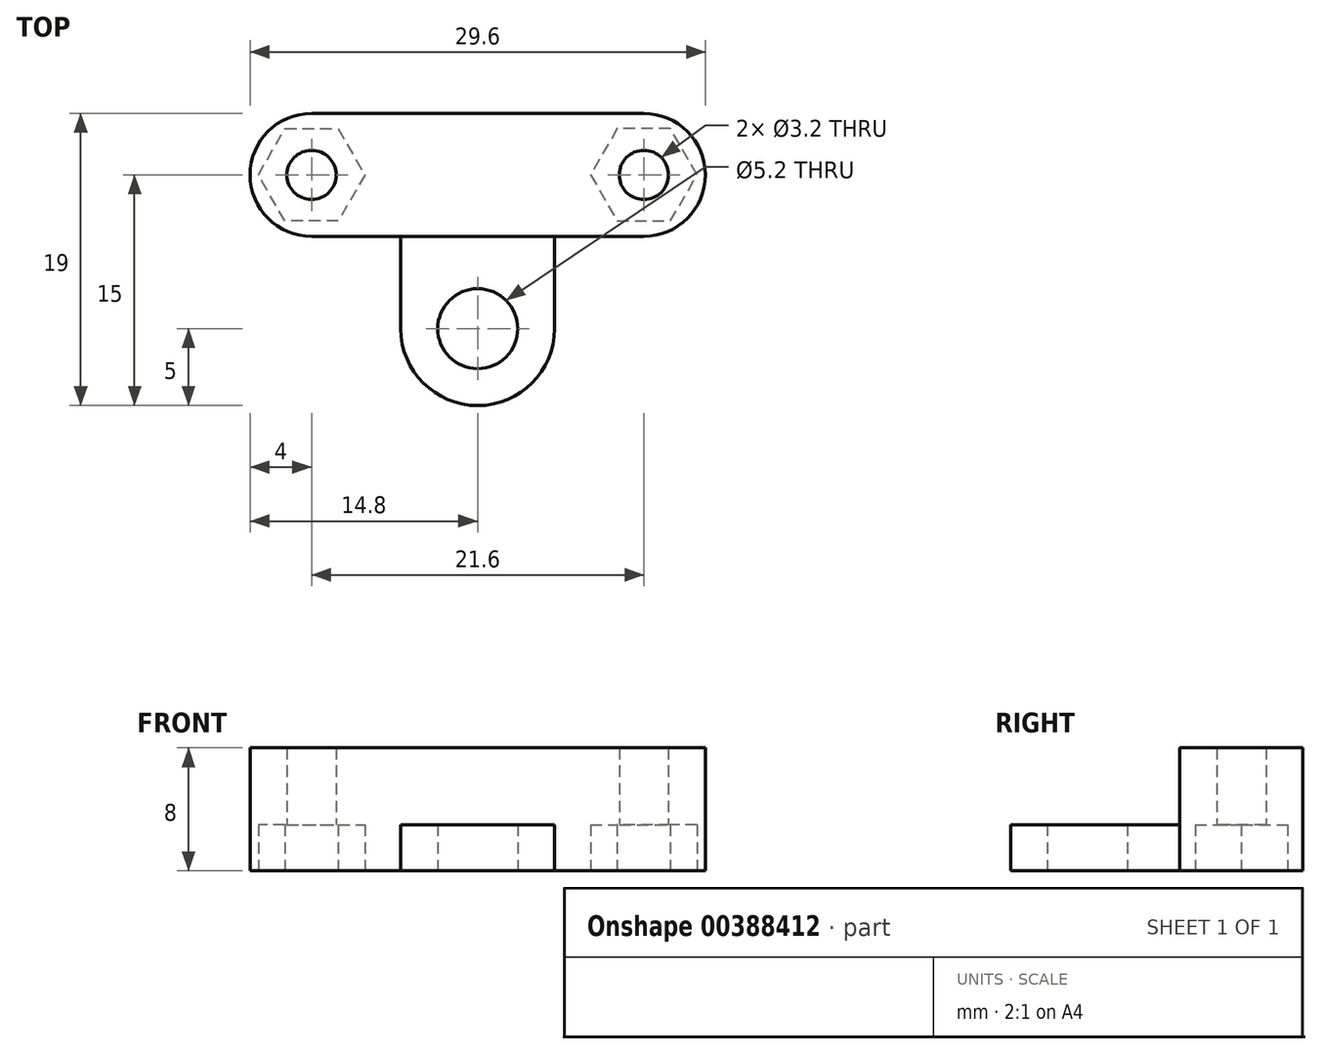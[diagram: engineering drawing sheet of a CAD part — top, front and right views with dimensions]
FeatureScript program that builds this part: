
annotation { "Feature Type Name" : "Feature", "Feature Type Description" : "" }
export const myFeature = defineFeature(function(context is Context, id is Id, definition is map)
    precondition{}
    {
        {
            var Q0;
            Q0=qCreatedBy(makeId("Top.planeOp"),FACE);
            var sketch = newSketch(context, id + "F0", { "sketchPlane" : qUnion([Q0])});
            skCircle(sketch, "E0", {"center": v(0, 0) * mm, "radius": 2.6 * mm});
            skArc(sketch, "E1", {"start": v(-5, 0) * mm, "mid": v(0, -5) * mm, "end": v(5, 0) * mm});
            skCircle(sketch, "E2", {"center": v(-10.8, 10) * mm, "radius": 1.6 * mm});
            skArc(sketch, "E3", {"start": v(-10.8, 14) * mm, "mid": v(-14.8, 10) * mm, "end": v(-10.8, 6) * mm});
            skLineSegment(sketch, "E4", {"start": v(-10.8, 14) * mm, "end": v(0, 14) * mm});
            skLineSegment(sketch, "E5", {"start": v(-10.8, 6) * mm, "end": v(-5, 6) * mm});
            skLineSegment(sketch, "E6", {"start": v(-5, 0) * mm, "end": v(-5, 6) * mm});
            skLineSegment(sketch, "E7", {"start": v(0, 0) * mm, "end": v(0, 14) * mm, "construction": true});
            skLineSegment(sketch, "E8.MirrorCS", {"start": v(10.8, 14) * mm, "end": v(0, 14) * mm});
            skLineSegment(sketch, "E9.MirrorCS", {"start": v(10.8, 6) * mm, "end": v(5, 6) * mm});
            skLineSegment(sketch, "E10.MirrorCS", {"start": v(5, 0) * mm, "end": v(5, 6) * mm});
            skArc(sketch, "E11.MirrorCS", {"start": v(10.8, 14) * mm, "mid": v(14.8, 10) * mm, "end": v(10.8, 6) * mm});
            skCircle(sketch, "E12.MirrorC", {"center": v(10.8, 10) * mm, "radius": 1.6 * mm});
            skSolve(sketch);
        }
        {
            var Q0;
            Q0 = qSketchRegion(id + "F0", true);
            extrude(context, id + "F1", {"entities" : qUnion([Q0]), "depth" : 3 * mm});
        }
        {
            var Q0;
            Q0=makeQuery(id+"F1.opExtrude","CAP_FACE",FACE,{"disambiguationData":[OSD([sQuery(id+"F0.wireOp",EDGE,"E0"),sQuery(id+"F0.wireOp",EDGE,"E1"),sQuery(id+"F0.wireOp",EDGE,"E2"),sQuery(id+"F0.wireOp",EDGE,"E3"),sQuery(id+"F0.wireOp",EDGE,"E4"),sQuery(id+"F0.wireOp",EDGE,"E5"),sQuery(id+"F0.wireOp",EDGE,"E6"),sQuery(id+"F0.wireOp",EDGE,"E8.MirrorCS"),sQuery(id+"F0.wireOp",EDGE,"E9.MirrorCS"),sQuery(id+"F0.wireOp",EDGE,"E10.MirrorCS"),sQuery(id+"F0.wireOp",EDGE,"E11.MirrorCS"),sQuery(id+"F0.wireOp",EDGE,"E12.MirrorC")])],"isStart":false});
            var sketch = newSketch(context, id + "F2", { "sketchPlane" : qUnion([Q0])});
            skLineSegment(sketch, "E13.0", {"start": v(10.8, 14) * mm, "end": v(-10.8, 14) * mm});
            skArc(sketch, "E14.0", {"start": v(-10.8, 14) * mm, "mid": v(-14.8, 10) * mm, "end": v(-10.8, 6) * mm});
            skLineSegment(sketch, "E15.0", {"start": v(-10.8, 6) * mm, "end": v(-5, 6) * mm});
            skLineSegment(sketch, "E16.0", {"start": v(10.8, 6) * mm, "end": v(5, 6) * mm});
            skArc(sketch, "E17.0", {"start": v(10.8, 14) * mm, "mid": v(14.8, 10) * mm, "end": v(10.8, 6) * mm});
            skLineSegment(sketch, "E18", {"start": v(-5, 6) * mm, "end": v(5, 6) * mm});
            skCircle(sketch, "E19.0", {"center": v(-10.8, 10) * mm, "radius": 1.6 * mm});
            skCircle(sketch, "E20.0", {"center": v(10.8, 10) * mm, "radius": 1.6 * mm});
            skSolve(sketch);
        }
        {
            var Q0;
            Q0 = qSketchRegion(id + "F2", true);
            extrude(context, id + "F3", {"entities" : qUnion([Q0]), "operationType" : NewBodyOperationType.ADD, "depth" : 5 * mm});
        }
        {
            var Q0;
            Q0=makeQuery(id+"F1.opExtrude","CAP_FACE",FACE,{"disambiguationData":[OSD([sQuery(id+"F0.wireOp",EDGE,"E0"),sQuery(id+"F0.wireOp",EDGE,"E1"),sQuery(id+"F0.wireOp",EDGE,"E2"),sQuery(id+"F0.wireOp",EDGE,"E3"),sQuery(id+"F0.wireOp",EDGE,"E4"),sQuery(id+"F0.wireOp",EDGE,"E5"),sQuery(id+"F0.wireOp",EDGE,"E6"),sQuery(id+"F0.wireOp",EDGE,"E8.MirrorCS"),sQuery(id+"F0.wireOp",EDGE,"E9.MirrorCS"),sQuery(id+"F0.wireOp",EDGE,"E10.MirrorCS"),sQuery(id+"F0.wireOp",EDGE,"E11.MirrorCS"),sQuery(id+"F0.wireOp",EDGE,"E12.MirrorC")])],"isStart":true});
            var sketch = newSketch(context, id + "F4", { "sketchPlane" : qUnion([Q0])});
            skCircle(sketch, "E21.cCircle", {"center": v(10.8, -10) * mm, "radius": 3 * mm, "construction": true});
            skLineSegment(sketch, "E21.0", {"start": v(12.53, -13) * mm, "end": v(9.07, -13) * mm});
            skLineSegment(sketch, "E21.1", {"start": v(9.07, -13) * mm, "end": v(7.34, -10) * mm});
            skLineSegment(sketch, "E21.2", {"start": v(7.34, -10) * mm, "end": v(9.07, -7) * mm});
            skLineSegment(sketch, "E21.3", {"start": v(9.07, -7) * mm, "end": v(12.53, -7) * mm});
            skLineSegment(sketch, "E21.4", {"start": v(12.53, -7) * mm, "end": v(14.26, -10) * mm});
            skLineSegment(sketch, "E21.5", {"start": v(14.26, -10) * mm, "end": v(12.53, -13) * mm});
            skPoint(sketch, "E21.0.midPoint", {"position": v(10.8, -13) * mm});
            skLineSegment(sketch, "E22", {"start": v(0, 0) * mm, "end": v(0, -14) * mm, "construction": true});
            skCircle(sketch, "E23.MirrorC", {"center": v(-10.8, -10) * mm, "radius": 3 * mm, "construction": true});
            skLineSegment(sketch, "E24.MirrorCS", {"start": v(-9.07, -13) * mm, "end": v(-7.34, -10) * mm});
            skLineSegment(sketch, "E25.MirrorCS", {"start": v(-12.53, -13) * mm, "end": v(-9.07, -13) * mm});
            skLineSegment(sketch, "E26.MirrorCS", {"start": v(-14.26, -10) * mm, "end": v(-12.53, -13) * mm});
            skLineSegment(sketch, "E27.MirrorCS", {"start": v(-12.53, -7) * mm, "end": v(-14.26, -10) * mm});
            skLineSegment(sketch, "E28.MirrorCS", {"start": v(-9.07, -7) * mm, "end": v(-12.53, -7) * mm});
            skLineSegment(sketch, "E29.MirrorCS", {"start": v(-7.34, -10) * mm, "end": v(-9.07, -7) * mm});
            skSolve(sketch);
        }
        {
            var Q0;
            Q0 = qSketchRegion(id + "F4", true);
            extrude(context, id + "F5", {"entities" : qUnion([Q0]), "operationType" : NewBodyOperationType.REMOVE, "oppositeDirection" : true, "depth" : 3 * mm});
        }
    });
